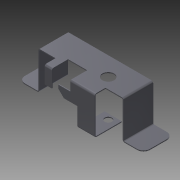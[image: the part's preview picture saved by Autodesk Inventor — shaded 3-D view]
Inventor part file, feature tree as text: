
AUTODESK INVENTOR PART (.ipt)
format: ipt  version: 2011 SP2 (Build 150309200, 309)  size: 299,520 bytes
history: native  units: mm
features: sheet_metal_op x15, other x9, sketch x8, hole x2, chamfer x1, projected_geometry x1
ambient origin geometry x8: Origin, YZ Plane, XZ Plane, XY Plane, X Axis, Y Axis, Z Axis, Center Point
bodies: Solid1 (feature_tree)
feature tree (36):
  sheet_metal_op  "Face1"
  sheet_metal_op  "Contour Flange1"
  sheet_metal_op  "Contour Flange2"
  sheet_metal_op  "Contour Flange3"
  sheet_metal_op  "Face2"
  other  "Corner Chamfer1"
  sheet_metal_op  "Contour Flange4"
  chamfer  "Corner Round1"
  sketch  "Sketch8"  dims[d10=41.0mm d11=22.0mm d12=1.0mm d13=0.5mm d14=2.0mm d15=1.0mm d16=1.0mm d17=1.0mm d18=4.0mm d19=1.0mm d20=1.0mm d21=41.0mm d22=22.0mm d23=1.0mm d24=0.5mm d25=2.0mm d26=1.0mm d27=1.0mm d28=1.0mm d29=4.0mm d30=1.0mm d31=1.0mm d32=42.0mm d33=30.0mm d34=1.0mm d35=0.5mm d36=2.0mm d37=1.0mm d38=1.0mm d39=1.0mm d40=4.0mm d41=1.0mm d42=1.0mm d43=19.0mm d44=19.0mm d45=1.0mm d46=0.0mm d47=10.0mm d48=40.0mm d49=1.0mm d50=1.0mm d51=0.5mm d52=2.0mm d53=1.0mm d54=6.0mm d55=6.0mm d56=45.0deg d57=19.0mm d58=1.0mm d59=0.5mm d60=2.0mm d61=1.0mm d62=1.0mm d63=1.0mm d64=4.0mm d65=1.0mm d66=1.0mm d67=7.0mm d68=22.0mm d69=9.0mm d70=13.0mm d71=6.0mm d72=4.0mm d73=2.0mm d74=90.0deg d75=1.0mm d76=20.594885mm d77=8.0mm d78=6.0mm d79=4.0mm d80=2.0mm d81=90.0deg d82=1.0mm d83=20.594885mm]
  hole  "Hole1"  [1 undecoded]
  hole  "Hole2"  [1 undecoded]
  sketch  "Sketch1"  dims[d0=95.0mm d1=32.0mm]
  other  "Plate1"
  sketch  "Sketch2"  dims[d2=19.0mm d4=8.0mm]
  other  "Plate2"
  sheet_metal_op  "Bend1"
  sheet_metal_op  "Corner1"
  sketch  "Sketch3"  dims[d5=27.0mm]
  other  "Plate3"
  sheet_metal_op  "Bend2"
  sheet_metal_op  "Corner2"
  sketch  "Sketch4"  dims[d6=26.0mm]
  other  "Plate4"
  sheet_metal_op  "Bend3"
  sheet_metal_op  "Corner3"
  sketch  "Sketch5"  dims[d7=44.0mm]
  projected_geometry  "Projected Loop1"
  sketch  "Sketch6"  dims[d8=20.0mm]
  other  "Plate5"
  sheet_metal_op  "Bend4"
  sketch  "Sketch7"  dims[d9=1.0mm]
  other  "Plate6"
  sheet_metal_op  "Bend5"
  sheet_metal_op  "Corner4"
  other  "Cut1"
  other  "Definition1"
note: 2 required parameter values undecoded (feature->parameter linkage not recoverable at this tier; creation-order binding heuristic only, values carry confidence <= 0.55)
